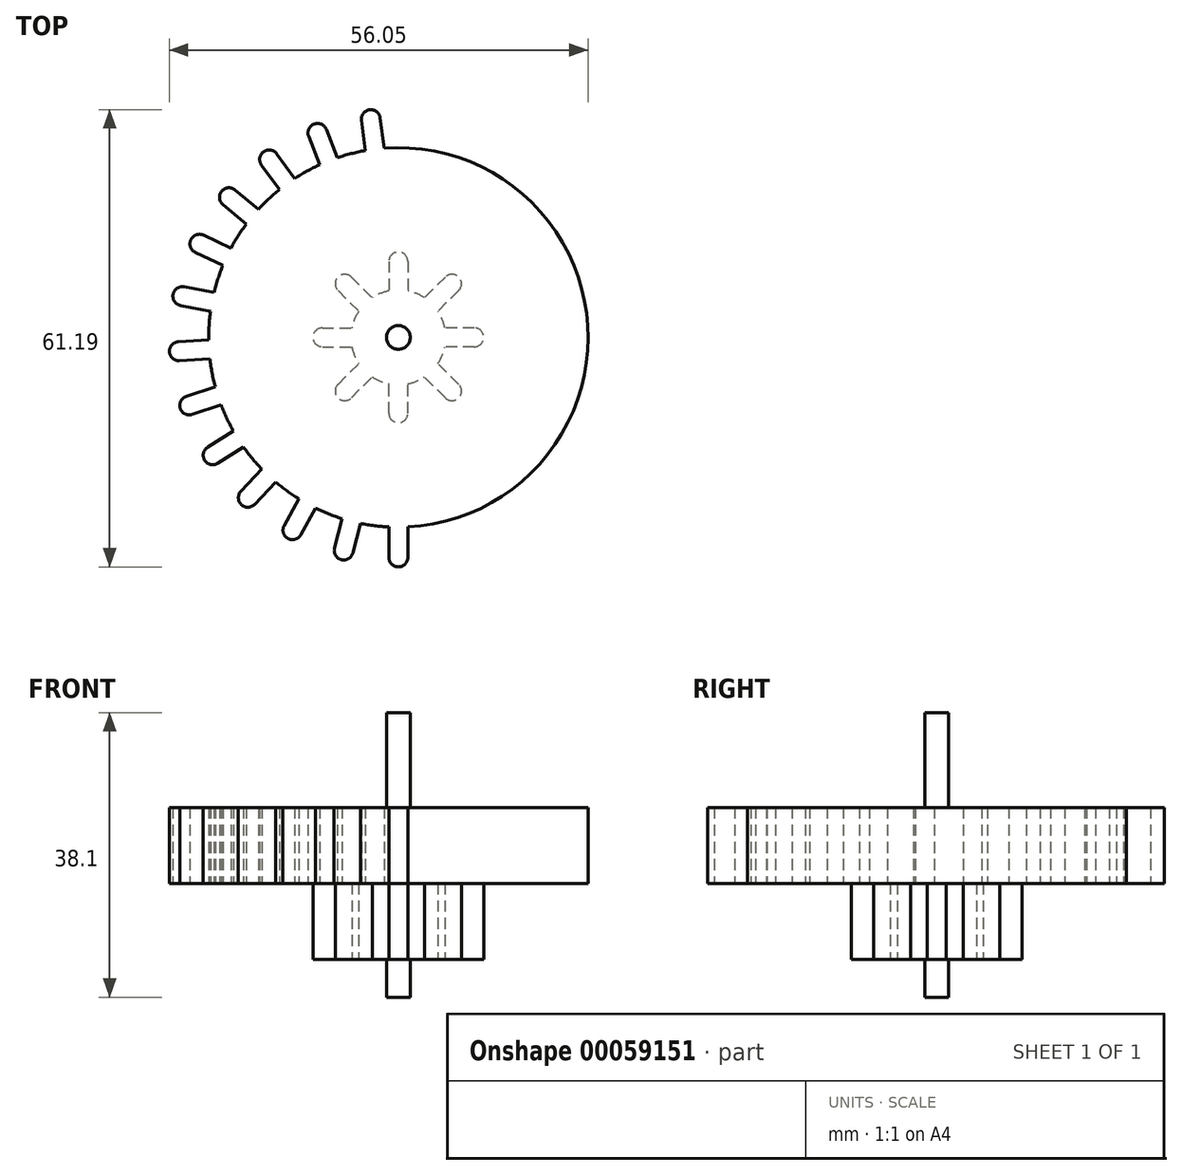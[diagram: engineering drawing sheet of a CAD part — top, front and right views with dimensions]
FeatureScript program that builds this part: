
annotation { "Feature Type Name" : "Feature", "Feature Type Description" : "" }
export const myFeature = defineFeature(function(context is Context, id is Id, definition is map)
    precondition{}
    {
        {
            var Q0;
            Q0=qCreatedBy(makeId("Top.planeOp"),FACE);
            var sketch = newSketch(context, id + "F0", { "sketchPlane" : qUnion([Q0])});
            skCircle(sketch, "E0", {"center": v(0, 0) * mm, "radius": 6.35 * mm});
            skLineSegment(sketch, "E1", {"start": v(0, 10.16) * mm, "end": v(1.27, 10.16) * mm});
            skLineSegment(sketch, "E2.MirrorCS", {"start": v(0, 10.16) * mm, "end": v(-1.27, 10.16) * mm});
            skLineSegment(sketch, "E3", {"start": v(-1.27, 10.16) * mm, "end": v(-1.27, 6.22) * mm});
            skLineSegment(sketch, "E4", {"start": v(1.27, 10.16) * mm, "end": v(1.27, 6.22) * mm});
            skArc(sketch, "E5", {"start": v(1.27, 10.16) * mm, "mid": v(0, 11.43) * mm, "end": v(-1.27, 10.16) * mm});
            skLineSegment(sketch, "E6.1.0", {"start": v(-6.29, 8.08) * mm, "end": v(-3.5, 5.3) * mm});
            skArc(sketch, "E6.1.1", {"start": v(-6.29, 8.08) * mm, "mid": v(-8.08, 8.08) * mm, "end": v(-8.08, 6.29) * mm});
            skLineSegment(sketch, "E6.1.2", {"start": v(-8.08, 6.29) * mm, "end": v(-5.3, 3.5) * mm});
            skLineSegment(sketch, "E6.2.0", {"start": v(-10.16, 1.27) * mm, "end": v(-6.22, 1.27) * mm});
            skArc(sketch, "E6.2.1", {"start": v(-10.16, 1.27) * mm, "mid": v(-11.43, 0) * mm, "end": v(-10.16, -1.27) * mm});
            skLineSegment(sketch, "E6.2.2", {"start": v(-10.16, -1.27) * mm, "end": v(-6.22, -1.27) * mm});
            skLineSegment(sketch, "E6.3.0", {"start": v(-8.08, -6.29) * mm, "end": v(-5.3, -3.5) * mm});
            skArc(sketch, "E6.3.1", {"start": v(-8.08, -6.29) * mm, "mid": v(-8.08, -8.08) * mm, "end": v(-6.29, -8.08) * mm});
            skLineSegment(sketch, "E6.3.2", {"start": v(-6.29, -8.08) * mm, "end": v(-3.5, -5.3) * mm});
            skLineSegment(sketch, "E6.4.0", {"start": v(-1.27, -10.16) * mm, "end": v(-1.27, -6.22) * mm});
            skArc(sketch, "E6.4.1", {"start": v(-1.27, -10.16) * mm, "mid": v(0, -11.43) * mm, "end": v(1.27, -10.16) * mm});
            skLineSegment(sketch, "E6.4.2", {"start": v(1.27, -10.16) * mm, "end": v(1.27, -6.22) * mm});
            skLineSegment(sketch, "E6.5.0", {"start": v(6.29, -8.08) * mm, "end": v(3.5, -5.3) * mm});
            skArc(sketch, "E6.5.1", {"start": v(6.29, -8.08) * mm, "mid": v(8.08, -8.08) * mm, "end": v(8.08, -6.29) * mm});
            skLineSegment(sketch, "E6.5.2", {"start": v(8.08, -6.29) * mm, "end": v(5.3, -3.5) * mm});
            skLineSegment(sketch, "E7.2.6.0", {"start": v(10.16, -1.27) * mm, "end": v(6.22, -1.27) * mm});
            skArc(sketch, "E7.3.6.0", {"start": v(10.16, -1.27) * mm, "mid": v(11.43, 0) * mm, "end": v(10.16, 1.27) * mm});
            skLineSegment(sketch, "E7.7.6.0", {"start": v(10.16, 1.27) * mm, "end": v(6.22, 1.27) * mm});
            skLineSegment(sketch, "E7.2.7.0", {"start": v(8.08, 6.29) * mm, "end": v(5.3, 3.5) * mm});
            skArc(sketch, "E7.3.7.0", {"start": v(8.08, 6.29) * mm, "mid": v(8.08, 8.08) * mm, "end": v(6.29, 8.08) * mm});
            skLineSegment(sketch, "E7.7.7.0", {"start": v(6.29, 8.08) * mm, "end": v(3.5, 5.3) * mm});
            skSolve(sketch);
        }
        {
            var Q0;
            {var subQ0=sQuery(id+"F0.wireOp",EDGE,"E0");var subQ3=makeQuery(id+"F0.imprint","INTERSECT",VERTEX,{"derivedFrom":[subQ0,sQuery(id+"F0.wireOp",EDGE,"E6.6.2")]});Q0=makeQuery(id+"F0.imprint","IMPRINT",FACE,{"disambiguationData":[TD([[makeQuery(id+"F0.imprint","IMPRINT",EDGE,{"disambiguationData":[TD([[subQ3,-1.0]])],"derivedFrom":subQ0}),1.0]])]});}
            var Q1;
            {var subQ0=sQuery(id+"F0.wireOp",EDGE,"E6.1.0");Q1=makeQuery(id+"F0.imprint","IMPRINT",FACE,{"disambiguationData":[TD([[makeQuery(id+"F0.imprint","IMPRINT",EDGE,{"derivedFrom":subQ0}),-1.0]])]});}
            var Q2;
            Q2=makeQuery(id+"F0.imprint","IMPRINT",FACE,{"disambiguationData":[TD([[makeQuery(id+"F0.imprint","IMPRINT",EDGE,{"derivedFrom":sQuery(id+"F0.wireOp",EDGE,"E1")}),-1.0]])]});
            var Q3;
            {var subQ0=sQuery(id+"F0.wireOp",EDGE,"E6.7.0");Q3=makeQuery(id+"F0.imprint","IMPRINT",FACE,{"disambiguationData":[TD([[makeQuery(id+"F0.imprint","IMPRINT",EDGE,{"derivedFrom":subQ0}),-1.0]])]});}
            var Q4;
            {var subQ0=sQuery(id+"F0.wireOp",EDGE,"E6.6.0");Q4=makeQuery(id+"F0.imprint","IMPRINT",FACE,{"disambiguationData":[TD([[makeQuery(id+"F0.imprint","IMPRINT",EDGE,{"derivedFrom":subQ0}),-1.0]])]});}
            var Q5;
            Q5=makeQuery(id+"F0.imprint","IMPRINT",FACE,{"disambiguationData":[TD([[makeQuery(id+"F0.imprint","IMPRINT",EDGE,{"derivedFrom":sQuery(id+"F0.wireOp",EDGE,"E1")}),1.0]])]});
            var Q6;
            {var subQ0=sQuery(id+"F0.wireOp",EDGE,"E6.2.0");Q6=makeQuery(id+"F0.imprint","IMPRINT",FACE,{"disambiguationData":[TD([[makeQuery(id+"F0.imprint","IMPRINT",EDGE,{"derivedFrom":subQ0}),-1.0]])]});}
            var Q7;
            {var subQ0=sQuery(id+"F0.wireOp",EDGE,"E6.3.0");Q7=makeQuery(id+"F0.imprint","IMPRINT",FACE,{"disambiguationData":[TD([[makeQuery(id+"F0.imprint","IMPRINT",EDGE,{"derivedFrom":subQ0}),-1.0]])]});}
            var Q8;
            {var subQ0=sQuery(id+"F0.wireOp",EDGE,"E6.4.0");Q8=makeQuery(id+"F0.imprint","IMPRINT",FACE,{"disambiguationData":[TD([[makeQuery(id+"F0.imprint","IMPRINT",EDGE,{"derivedFrom":subQ0}),-1.0]])]});}
            var Q9;
            {var subQ0=sQuery(id+"F0.wireOp",EDGE,"E6.5.0");Q9=makeQuery(id+"F0.imprint","IMPRINT",FACE,{"disambiguationData":[TD([[makeQuery(id+"F0.imprint","IMPRINT",EDGE,{"derivedFrom":subQ0}),-1.0]])]});}
            var Q10;
            {var subQ0=sQuery(id+"F0.wireOp",EDGE,"E7.2.6.0");Q10=makeQuery(id+"F0.imprint","IMPRINT",FACE,{"disambiguationData":[TD([[makeQuery(id+"F0.imprint","IMPRINT",EDGE,{"derivedFrom":subQ0}),-1.0]])]});}
            var Q11;
            {var subQ0=sQuery(id+"F0.wireOp",EDGE,"E7.2.7.0");Q11=makeQuery(id+"F0.imprint","IMPRINT",FACE,{"disambiguationData":[TD([[makeQuery(id+"F0.imprint","IMPRINT",EDGE,{"derivedFrom":subQ0}),-1.0]])]});}
            extrude(context, id + "F1", {"entities" : qUnion([Q0, Q1, Q2, Q3, Q4, Q5, Q6, Q7, Q8, Q9, Q10, Q11]), "depth" : 10.16 * mm});
        }
        {
            var Q0;
            Q0=makeQuery(id+"F1.opExtrude","CAP_FACE",FACE,{"disambiguationData":[OSD([sQuery(id+"F0.wireOp",EDGE,"E0"),sQuery(id+"F0.wireOp",EDGE,"E3"),sQuery(id+"F0.wireOp",EDGE,"E4"),sQuery(id+"F0.wireOp",EDGE,"E5"),sQuery(id+"F0.wireOp",EDGE,"E6.1.0"),sQuery(id+"F0.wireOp",EDGE,"E6.1.1"),sQuery(id+"F0.wireOp",EDGE,"E6.1.2"),sQuery(id+"F0.wireOp",EDGE,"E6.2.0"),sQuery(id+"F0.wireOp",EDGE,"E6.2.1"),sQuery(id+"F0.wireOp",EDGE,"E6.2.2"),sQuery(id+"F0.wireOp",EDGE,"E6.3.0"),sQuery(id+"F0.wireOp",EDGE,"E6.3.1"),sQuery(id+"F0.wireOp",EDGE,"E6.3.2"),sQuery(id+"F0.wireOp",EDGE,"E6.4.0"),sQuery(id+"F0.wireOp",EDGE,"E6.4.1"),sQuery(id+"F0.wireOp",EDGE,"E6.4.2"),sQuery(id+"F0.wireOp",EDGE,"E6.5.0"),sQuery(id+"F0.wireOp",EDGE,"E6.5.1"),sQuery(id+"F0.wireOp",EDGE,"E6.5.2"),sQuery(id+"F0.wireOp",EDGE,"E6.6.0"),sQuery(id+"F0.wireOp",EDGE,"E6.6.1"),sQuery(id+"F0.wireOp",EDGE,"E6.6.2"),sQuery(id+"F0.wireOp",EDGE,"E6.7.0"),sQuery(id+"F0.wireOp",EDGE,"E6.7.1"),sQuery(id+"F0.wireOp",EDGE,"E6.7.2")])],"isStart":false});
            var sketch = newSketch(context, id + "F2", { "sketchPlane" : qUnion([Q0])});
            skPoint(sketch, "E8.center", {"position": v(0, 0) * mm});
            skCircle(sketch, "E9", {"center": v(0, 0) * mm, "radius": 25.4 * mm});
            skLineSegment(sketch, "E8.17.0", {"start": v(28.4, -7.9) * mm, "end": v(24.52, -6.63) * mm});
            skLineSegment(sketch, "E8.17.1", {"start": v(27.6, -10.3) * mm, "end": v(23.73, -9.05) * mm});
            skArc(sketch, "E8.17.2", {"start": v(27.6, -10.3) * mm, "mid": v(29.2, -9.5) * mm, "end": v(28.4, -7.9) * mm});
            skLineSegment(sketch, "E8.14.0", {"start": v(15.3, -25.19) * mm, "end": v(13.33, -21.62) * mm});
            skLineSegment(sketch, "E8.14.1", {"start": v(13.07, -26.41) * mm, "end": v(11.1, -22.84) * mm});
            skArc(sketch, "E8.14.2", {"start": v(13.07, -26.41) * mm, "mid": v(14.8, -26.91) * mm, "end": v(15.3, -25.19) * mm});
            skLineSegment(sketch, "E8.4.0", {"start": v(-27.18, 11.39) * mm, "end": v(-23.5, 9.65) * mm});
            skLineSegment(sketch, "E8.1.0", {"start": v(-12.02, 26.9) * mm, "end": v(-10.52, 23.12) * mm});
            skLineSegment(sketch, "E8.1.1", {"start": v(-9.66, 27.84) * mm, "end": v(-8.16, 24.05) * mm});
            skArc(sketch, "E8.1.2", {"start": v(-9.66, 27.84) * mm, "mid": v(-11.3, 28.56) * mm, "end": v(-12.02, 26.9) * mm});
            skLineSegment(sketch, "E8.2.0", {"start": v(-18.33, 23.07) * mm, "end": v(-15.94, 19.78) * mm});
            skLineSegment(sketch, "E8.2.1", {"start": v(-16.28, 24.57) * mm, "end": v(-13.88, 21.27) * mm});
            skArc(sketch, "E8.2.2", {"start": v(-16.28, 24.57) * mm, "mid": v(-18.05, 24.85) * mm, "end": v(-18.33, 23.07) * mm});
            skLineSegment(sketch, "E8.4.1", {"start": v(-26.1, 13.68) * mm, "end": v(-22.41, 11.95) * mm});
            skArc(sketch, "E8.4.2", {"start": v(-26.1, 13.68) * mm, "mid": v(-27.79, 13.08) * mm, "end": v(-27.18, 11.39) * mm});
            skLineSegment(sketch, "E8.5.1", {"start": v(-28.68, 6.76) * mm, "end": v(-24.68, 6) * mm});
            skLineSegment(sketch, "E10.3.21.0", {"start": v(23.5, 17.79) * mm, "end": v(20.36, 15.2) * mm});
            skLineSegment(sketch, "E8.16.0", {"start": v(25.54, -14.7) * mm, "end": v(22.1, -12.52) * mm});
            skArc(sketch, "E8.10.2", {"start": v(-15.3, -25.19) * mm, "mid": v(-14.8, -26.91) * mm, "end": v(-13.07, -26.41) * mm});
            skArc(sketch, "E8.5.2", {"start": v(-28.68, 6.76) * mm, "mid": v(-30.17, 5.75) * mm, "end": v(-29.16, 4.27) * mm});
            skArc(sketch, "E10.6.21.0", {"start": v(23.5, 17.79) * mm, "mid": v(23.66, 19.58) * mm, "end": v(21.88, 19.75) * mm});
            skLineSegment(sketch, "E8.16.1", {"start": v(24.18, -16.85) * mm, "end": v(20.74, -14.67) * mm});
            skLineSegment(sketch, "E8.11.0", {"start": v(-6.1, -28.83) * mm, "end": v(-5.08, -24.89) * mm});
            skArc(sketch, "E8.16.2", {"start": v(24.18, -16.85) * mm, "mid": v(25.93, -16.46) * mm, "end": v(25.54, -14.7) * mm});
            skLineSegment(sketch, "E8.11.1", {"start": v(-8.55, -28.2) * mm, "end": v(-7.54, -24.26) * mm});
            skArc(sketch, "E8.11.2", {"start": v(-8.55, -28.2) * mm, "mid": v(-7.64, -29.75) * mm, "end": v(-6.1, -28.83) * mm});
            skLineSegment(sketch, "E8.12.0", {"start": v(1.27, -29.44) * mm, "end": v(1.27, -25.37) * mm});
            skLineSegment(sketch, "E8.12.1", {"start": v(-1.27, -29.44) * mm, "end": v(-1.27, -25.37) * mm});
            skLineSegment(sketch, "E8.7.0", {"start": v(-27.6, -10.3) * mm, "end": v(-23.73, -9.05) * mm});
            skLineSegment(sketch, "E8.18.0", {"start": v(29.46, -0.58) * mm, "end": v(25.4, -0.33) * mm});
            skArc(sketch, "E8.12.2", {"start": v(-1.27, -29.44) * mm, "mid": v(0, -30.71) * mm, "end": v(1.27, -29.44) * mm});
            skLineSegment(sketch, "E8.18.1", {"start": v(29.3, -3.12) * mm, "end": v(25.24, -2.86) * mm});
            skLineSegment(sketch, "E8.13.0", {"start": v(8.55, -28.2) * mm, "end": v(7.54, -24.26) * mm});
            skArc(sketch, "E8.7.2", {"start": v(-28.4, -7.9) * mm, "mid": v(-29.2, -9.5) * mm, "end": v(-27.6, -10.3) * mm});
            skArc(sketch, "E8.18.2", {"start": v(29.3, -3.12) * mm, "mid": v(30.65, -1.93) * mm, "end": v(29.46, -0.58) * mm});
            skLineSegment(sketch, "E8.13.1", {"start": v(6.1, -28.83) * mm, "end": v(5.08, -24.89) * mm});
            skLineSegment(sketch, "E8.8.0", {"start": v(-24.18, -16.85) * mm, "end": v(-20.74, -14.67) * mm});
            skLineSegment(sketch, "E11.2.24.0", {"start": v(2.43, 29.37) * mm, "end": v(1.92, 25.33) * mm});
            skArc(sketch, "E11.6.24.0", {"start": v(4.95, 29.05) * mm, "mid": v(3.85, 30.47) * mm, "end": v(2.43, 29.37) * mm});
            skArc(sketch, "E8.8.2", {"start": v(-25.54, -14.7) * mm, "mid": v(-25.93, -16.46) * mm, "end": v(-24.18, -16.85) * mm});
            skArc(sketch, "E8.13.2", {"start": v(6.1, -28.83) * mm, "mid": v(7.64, -29.75) * mm, "end": v(8.55, -28.2) * mm});
            skLineSegment(sketch, "E8.8.1", {"start": v(-25.54, -14.7) * mm, "end": v(-22.1, -12.52) * mm});
            skLineSegment(sketch, "E11.3.24.0", {"start": v(4.95, 29.05) * mm, "end": v(4.44, 25) * mm});
            skLineSegment(sketch, "E8.9.0", {"start": v(-19.23, -22.33) * mm, "end": v(-16.44, -19.36) * mm});
            skLineSegment(sketch, "E10.2.20.0", {"start": v(26.1, 13.68) * mm, "end": v(22.41, 11.95) * mm});
            skLineSegment(sketch, "E8.9.1", {"start": v(-21.08, -20.6) * mm, "end": v(-18.3, -17.62) * mm});
            skLineSegment(sketch, "E8.3.1", {"start": v(-21.88, 19.75) * mm, "end": v(-18.74, 17.15) * mm});
            skArc(sketch, "E8.3.2", {"start": v(-21.88, 19.75) * mm, "mid": v(-23.66, 19.58) * mm, "end": v(-23.5, 17.79) * mm});
            skLineSegment(sketch, "E8.3.0", {"start": v(-23.5, 17.79) * mm, "end": v(-20.36, 15.2) * mm});
            skLineSegment(sketch, "E8.15.0", {"start": v(21.08, -20.6) * mm, "end": v(18.3, -17.62) * mm});
            skArc(sketch, "E8.9.2", {"start": v(-21.08, -20.6) * mm, "mid": v(-21.02, -22.39) * mm, "end": v(-19.23, -22.33) * mm});
            skArc(sketch, "E10.6.20.0", {"start": v(27.18, 11.39) * mm, "mid": v(27.79, 13.08) * mm, "end": v(26.1, 13.68) * mm});
            skLineSegment(sketch, "E8.15.1", {"start": v(19.23, -22.33) * mm, "end": v(16.44, -19.36) * mm});
            skLineSegment(sketch, "E8.10.0", {"start": v(-13.07, -26.41) * mm, "end": v(-11.1, -22.84) * mm});
            skLineSegment(sketch, "E8.5.0", {"start": v(-29.16, 4.27) * mm, "end": v(-25.16, 3.5) * mm});
            skLineSegment(sketch, "E10.2.21.0", {"start": v(21.88, 19.75) * mm, "end": v(18.74, 17.15) * mm});
            skArc(sketch, "E8.15.2", {"start": v(19.23, -22.33) * mm, "mid": v(21.02, -22.39) * mm, "end": v(21.08, -20.6) * mm});
            skLineSegment(sketch, "E8.10.1", {"start": v(-15.3, -25.19) * mm, "end": v(-13.33, -21.62) * mm});
            skLineSegment(sketch, "E8.6.0", {"start": v(-29.3, -3.12) * mm, "end": v(-25.24, -2.86) * mm});
            skLineSegment(sketch, "E11.2.22.0", {"start": v(16.28, 24.57) * mm, "end": v(13.88, 21.27) * mm});
            skLineSegment(sketch, "E8.6.1", {"start": v(-29.46, -0.58) * mm, "end": v(-25.4, -0.33) * mm});
            skLineSegment(sketch, "E11.3.22.0", {"start": v(18.33, 23.07) * mm, "end": v(15.94, 19.78) * mm});
            skArc(sketch, "E8.6.2", {"start": v(-29.46, -0.58) * mm, "mid": v(-30.65, -1.93) * mm, "end": v(-29.3, -3.12) * mm});
            skArc(sketch, "E11.6.22.0", {"start": v(18.33, 23.07) * mm, "mid": v(18.05, 24.85) * mm, "end": v(16.28, 24.57) * mm});
            skLineSegment(sketch, "E11.2.23.0", {"start": v(9.66, 27.84) * mm, "end": v(8.16, 24.05) * mm});
            skLineSegment(sketch, "E8.7.1", {"start": v(-28.4, -7.9) * mm, "end": v(-24.52, -6.63) * mm});
            skLineSegment(sketch, "E11.3.23.0", {"start": v(12.02, 26.9) * mm, "end": v(10.52, 23.12) * mm});
            skArc(sketch, "E11.6.23.0", {"start": v(12.02, 26.9) * mm, "mid": v(11.3, 28.56) * mm, "end": v(9.66, 27.84) * mm});
            skLineSegment(sketch, "E8.19.1", {"start": v(29.16, 4.27) * mm, "end": v(25.16, 3.5) * mm});
            skLineSegment(sketch, "E8.19.0", {"start": v(28.68, 6.76) * mm, "end": v(24.68, 6) * mm});
            skArc(sketch, "E8.19.2", {"start": v(29.16, 4.27) * mm, "mid": v(30.17, 5.75) * mm, "end": v(28.68, 6.76) * mm});
            skLineSegment(sketch, "E12", {"start": v(-4.95, 29.05) * mm, "end": v(-4.44, 25) * mm});
            skLineSegment(sketch, "E13", {"start": v(-2.43, 29.37) * mm, "end": v(-1.92, 25.33) * mm});
            skArc(sketch, "E14", {"start": v(-2.43, 29.37) * mm, "mid": v(-3.85, 30.47) * mm, "end": v(-4.95, 29.05) * mm});
            skLineSegment(sketch, "E10.3.20.0", {"start": v(27.18, 11.39) * mm, "end": v(23.5, 9.65) * mm});
            skLineSegment(sketch, "E15", {"start": v(-3.7, 29.2) * mm, "end": v(-4.95, 29.05) * mm});
            skLineSegment(sketch, "E16.MirrorCS", {"start": v(-3.7, 29.21) * mm, "end": v(-2.43, 29.37) * mm});
            skSolve(sketch);
        }
        {
            var Q0;
            {var subQ5=sQuery(id+"F2.wireOp",EDGE,"b0236bb4-0209-4acc-8ecc-2f9dec660ae4.1.2");Q0=makeQuery(id+"F2.imprint","IMPRINT",FACE,{"disambiguationData":[TD([[makeQuery(id+"F2.imprint","IMPRINT",EDGE,{"derivedFrom":subQ5}),1.0]])]});}
            var Q1;
            {var subQ5=sQuery(id+"F2.wireOp",EDGE,"b0236bb4-0209-4acc-8ecc-2f9dec660ae4.2.2");Q1=makeQuery(id+"F2.imprint","IMPRINT",FACE,{"disambiguationData":[TD([[makeQuery(id+"F2.imprint","IMPRINT",EDGE,{"derivedFrom":subQ5}),1.0]])]});}
            var Q2;
            {var subQ5=sQuery(id+"F2.wireOp",EDGE,"b0236bb4-0209-4acc-8ecc-2f9dec660ae4.3.2");Q2=makeQuery(id+"F2.imprint","IMPRINT",FACE,{"disambiguationData":[TD([[makeQuery(id+"F2.imprint","IMPRINT",EDGE,{"derivedFrom":subQ5}),1.0]])]});}
            var Q3;
            {var subQ5=sQuery(id+"F2.wireOp",EDGE,"b0236bb4-0209-4acc-8ecc-2f9dec660ae4.4.2");Q3=makeQuery(id+"F2.imprint","IMPRINT",FACE,{"disambiguationData":[TD([[makeQuery(id+"F2.imprint","IMPRINT",EDGE,{"derivedFrom":subQ5}),1.0]])]});}
            var Q4;
            {var subQ5=sQuery(id+"F2.wireOp",EDGE,"b0236bb4-0209-4acc-8ecc-2f9dec660ae4.5.2");Q4=makeQuery(id+"F2.imprint","IMPRINT",FACE,{"disambiguationData":[TD([[makeQuery(id+"F2.imprint","IMPRINT",EDGE,{"derivedFrom":subQ5}),1.0]])]});}
            var Q5;
            {var subQ5=sQuery(id+"F2.wireOp",EDGE,"b0236bb4-0209-4acc-8ecc-2f9dec660ae4.6.2");Q5=makeQuery(id+"F2.imprint","IMPRINT",FACE,{"disambiguationData":[TD([[makeQuery(id+"F2.imprint","IMPRINT",EDGE,{"derivedFrom":subQ5}),1.0]])]});}
            var Q6;
            {var subQ5=sQuery(id+"F2.wireOp",EDGE,"b0236bb4-0209-4acc-8ecc-2f9dec660ae4.7.2");Q6=makeQuery(id+"F2.imprint","IMPRINT",FACE,{"disambiguationData":[TD([[makeQuery(id+"F2.imprint","IMPRINT",EDGE,{"derivedFrom":subQ5}),1.0]])]});}
            var Q7;
            {var subQ5=sQuery(id+"F2.wireOp",EDGE,"b0236bb4-0209-4acc-8ecc-2f9dec660ae4.8.2");Q7=makeQuery(id+"F2.imprint","IMPRINT",FACE,{"disambiguationData":[TD([[makeQuery(id+"F2.imprint","IMPRINT",EDGE,{"derivedFrom":subQ5}),1.0]])]});}
            var Q8;
            {var subQ5=sQuery(id+"F2.wireOp",EDGE,"b0236bb4-0209-4acc-8ecc-2f9dec660ae4.9.2");Q8=makeQuery(id+"F2.imprint","IMPRINT",FACE,{"disambiguationData":[TD([[makeQuery(id+"F2.imprint","IMPRINT",EDGE,{"derivedFrom":subQ5}),1.0]])]});}
            var Q9;
            {var subQ5=sQuery(id+"F2.wireOp",EDGE,"b0236bb4-0209-4acc-8ecc-2f9dec660ae4.10.2");Q9=makeQuery(id+"F2.imprint","IMPRINT",FACE,{"disambiguationData":[TD([[makeQuery(id+"F2.imprint","IMPRINT",EDGE,{"derivedFrom":subQ5}),1.0]])]});}
            var Q10;
            {var subQ5=sQuery(id+"F2.wireOp",EDGE,"b0236bb4-0209-4acc-8ecc-2f9dec660ae4.11.2");Q10=makeQuery(id+"F2.imprint","IMPRINT",FACE,{"disambiguationData":[TD([[makeQuery(id+"F2.imprint","IMPRINT",EDGE,{"derivedFrom":subQ5}),1.0]])]});}
            var Q11;
            Q11=makeQuery(id+"F2.imprint","IMPRINT",FACE,{"disambiguationData":[TD([[makeQuery(id+"F2.imprint","IMPRINT",EDGE,{"derivedFrom":sQuery(id+"F2.wireOp",EDGE,"a617dc30-04bb-4b02-898b-82f21cb4bea1")}),1.0]])]});
            var Q12;
            {var subQ11=sQuery(id+"F0.wireOp",EDGE,"E3");Q12=makeQuery(id+"F2.imprint","IMPRINT",FACE,{"disambiguationData":[TD([[makeQuery(id+"F2.imprint","IMPRINT",EDGE,{"derivedFrom":makeQuery(id+"F1.opExtrude","CAP_EDGE",EDGE,{"disambiguationData":[OSD([subQ11])],"isStart":false})}),1.0]])]});}
            var Q13;
            {var subQ1=sQuery(id+"F2.wireOp",EDGE,"a3267446-eaba-4b86-878d-2723d5209084");Q13=makeQuery(id+"F2.imprint","IMPRINT",FACE,{"disambiguationData":[TD([[makeQuery(id+"F2.imprint","IMPRINT",EDGE,{"derivedFrom":subQ1}),1.0]])]});}
            var Q14;
            {var subQ22=sQuery(id+"F0.wireOp",EDGE,"E3");Q14=makeQuery(id+"F2.imprint","IMPRINT",FACE,{"disambiguationData":[TD([[makeQuery(id+"F2.imprint","IMPRINT",EDGE,{"derivedFrom":makeQuery(id+"F1.opExtrude","CAP_EDGE",EDGE,{"disambiguationData":[OSD([subQ22])],"isStart":false})}),-1.0]])]});}
            var Q15;
            {var subQ5=sQuery(id+"F2.wireOp",EDGE,"b0236bb4-0209-4acc-8ecc-2f9dec660ae4.12.2");Q15=makeQuery(id+"F2.imprint","IMPRINT",FACE,{"disambiguationData":[TD([[makeQuery(id+"F2.imprint","IMPRINT",EDGE,{"derivedFrom":subQ5}),1.0]])]});}
            var Q16;
            {var subQ5=sQuery(id+"F2.wireOp",EDGE,"E8.4.2");Q16=makeQuery(id+"F2.imprint","IMPRINT",FACE,{"disambiguationData":[TD([[makeQuery(id+"F2.imprint","IMPRINT",EDGE,{"derivedFrom":subQ5}),1.0]])]});}
            var Q17;
            {var subQ5=sQuery(id+"F2.wireOp",EDGE,"E8.3.2");Q17=makeQuery(id+"F2.imprint","IMPRINT",FACE,{"disambiguationData":[TD([[makeQuery(id+"F2.imprint","IMPRINT",EDGE,{"derivedFrom":subQ5}),1.0]])]});}
            var Q18;
            {var subQ5=sQuery(id+"F2.wireOp",EDGE,"E8.2.2");Q18=makeQuery(id+"F2.imprint","IMPRINT",FACE,{"disambiguationData":[TD([[makeQuery(id+"F2.imprint","IMPRINT",EDGE,{"derivedFrom":subQ5}),1.0]])]});}
            var Q19;
            {var subQ5=sQuery(id+"F2.wireOp",EDGE,"E8.1.2");Q19=makeQuery(id+"F2.imprint","IMPRINT",FACE,{"disambiguationData":[TD([[makeQuery(id+"F2.imprint","IMPRINT",EDGE,{"derivedFrom":subQ5}),1.0]])]});}
            var Q20;
            {var subQ1=sQuery(id+"F2.wireOp",EDGE,"E12");Q20=makeQuery(id+"F2.imprint","IMPRINT",FACE,{"disambiguationData":[TD([[makeQuery(id+"F2.imprint","IMPRINT",EDGE,{"derivedFrom":subQ1}),1.0]])]});}
            var Q21;
            {var subQ5=sQuery(id+"F2.wireOp",EDGE,"E8.5.2");Q21=makeQuery(id+"F2.imprint","IMPRINT",FACE,{"disambiguationData":[TD([[makeQuery(id+"F2.imprint","IMPRINT",EDGE,{"derivedFrom":subQ5}),1.0]])]});}
            var Q22;
            {var subQ5=sQuery(id+"F2.wireOp",EDGE,"E8.6.2");Q22=makeQuery(id+"F2.imprint","IMPRINT",FACE,{"disambiguationData":[TD([[makeQuery(id+"F2.imprint","IMPRINT",EDGE,{"derivedFrom":subQ5}),1.0]])]});}
            var Q23;
            {var subQ5=sQuery(id+"F2.wireOp",EDGE,"E8.7.2");Q23=makeQuery(id+"F2.imprint","IMPRINT",FACE,{"disambiguationData":[TD([[makeQuery(id+"F2.imprint","IMPRINT",EDGE,{"derivedFrom":subQ5}),1.0]])]});}
            var Q24;
            {var subQ5=sQuery(id+"F2.wireOp",EDGE,"E8.8.2");Q24=makeQuery(id+"F2.imprint","IMPRINT",FACE,{"disambiguationData":[TD([[makeQuery(id+"F2.imprint","IMPRINT",EDGE,{"derivedFrom":subQ5}),1.0]])]});}
            var Q25;
            {var subQ5=sQuery(id+"F2.wireOp",EDGE,"E8.9.2");Q25=makeQuery(id+"F2.imprint","IMPRINT",FACE,{"disambiguationData":[TD([[makeQuery(id+"F2.imprint","IMPRINT",EDGE,{"derivedFrom":subQ5}),1.0]])]});}
            var Q26;
            {var subQ5=sQuery(id+"F2.wireOp",EDGE,"E8.10.2");Q26=makeQuery(id+"F2.imprint","IMPRINT",FACE,{"disambiguationData":[TD([[makeQuery(id+"F2.imprint","IMPRINT",EDGE,{"derivedFrom":subQ5}),1.0]])]});}
            var Q27;
            {var subQ5=sQuery(id+"F2.wireOp",EDGE,"E8.11.2");Q27=makeQuery(id+"F2.imprint","IMPRINT",FACE,{"disambiguationData":[TD([[makeQuery(id+"F2.imprint","IMPRINT",EDGE,{"derivedFrom":subQ5}),1.0]])]});}
            var Q28;
            {var subQ5=sQuery(id+"F2.wireOp",EDGE,"E8.12.2");Q28=makeQuery(id+"F2.imprint","IMPRINT",FACE,{"disambiguationData":[TD([[makeQuery(id+"F2.imprint","IMPRINT",EDGE,{"derivedFrom":subQ5}),1.0]])]});}
            var Q29;
            Q29=makeQuery(id+"F2.imprint","IMPRINT",FACE,{"disambiguationData":[TD([[makeQuery(id+"F2.imprint","IMPRINT",EDGE,{"derivedFrom":sQuery(id+"F2.wireOp",EDGE,"E14")}),1.0]])]});
            extrude(context, id + "F3", {"entities" : qUnion([Q0, Q1, Q2, Q3, Q4, Q5, Q6, Q7, Q8, Q9, Q10, Q11, Q12, Q13, Q14, Q15, Q16, Q17, Q18, Q19, Q20, Q21, Q22, Q23, Q24, Q25, Q26, Q27, Q28, Q29]), "operationType" : NewBodyOperationType.ADD, "depth" : 10.16 * mm});
        }
        {
            var Q0;
            Q0=makeQuery(id+"F3.opExtrude","CAP_FACE",FACE,{"disambiguationData":[OSD([sQuery(id+"F2.wireOp",EDGE,"E9"),sQuery(id+"F2.wireOp",EDGE,"E8.4.0"),sQuery(id+"F2.wireOp",EDGE,"E8.1.0"),sQuery(id+"F2.wireOp",EDGE,"E8.1.1"),sQuery(id+"F2.wireOp",EDGE,"E8.1.2"),sQuery(id+"F2.wireOp",EDGE,"E8.2.0"),sQuery(id+"F2.wireOp",EDGE,"E8.2.1"),sQuery(id+"F2.wireOp",EDGE,"E8.2.2"),sQuery(id+"F2.wireOp",EDGE,"E8.4.1"),sQuery(id+"F2.wireOp",EDGE,"E8.4.2"),sQuery(id+"F2.wireOp",EDGE,"E8.5.1"),sQuery(id+"F2.wireOp",EDGE,"E8.10.2"),sQuery(id+"F2.wireOp",EDGE,"E8.5.2"),sQuery(id+"F2.wireOp",EDGE,"E8.11.0"),sQuery(id+"F2.wireOp",EDGE,"E8.11.1"),sQuery(id+"F2.wireOp",EDGE,"E8.11.2"),sQuery(id+"F2.wireOp",EDGE,"E8.12.0"),sQuery(id+"F2.wireOp",EDGE,"E8.12.1"),sQuery(id+"F2.wireOp",EDGE,"E8.7.0"),sQuery(id+"F2.wireOp",EDGE,"E8.12.2"),sQuery(id+"F2.wireOp",EDGE,"E8.7.2"),sQuery(id+"F2.wireOp",EDGE,"E8.8.0"),sQuery(id+"F2.wireOp",EDGE,"E8.8.2"),sQuery(id+"F2.wireOp",EDGE,"E8.8.1"),sQuery(id+"F2.wireOp",EDGE,"E8.9.0"),sQuery(id+"F2.wireOp",EDGE,"E8.9.1"),sQuery(id+"F2.wireOp",EDGE,"E8.3.1"),sQuery(id+"F2.wireOp",EDGE,"E8.3.2"),sQuery(id+"F2.wireOp",EDGE,"E8.3.0"),sQuery(id+"F2.wireOp",EDGE,"E8.9.2"),sQuery(id+"F2.wireOp",EDGE,"E8.10.0"),sQuery(id+"F2.wireOp",EDGE,"E8.5.0"),sQuery(id+"F2.wireOp",EDGE,"E8.10.1"),sQuery(id+"F2.wireOp",EDGE,"E8.6.0"),sQuery(id+"F2.wireOp",EDGE,"E8.6.1"),sQuery(id+"F2.wireOp",EDGE,"E8.6.2"),sQuery(id+"F2.wireOp",EDGE,"E8.7.1"),sQuery(id+"F2.wireOp",EDGE,"E12"),sQuery(id+"F2.wireOp",EDGE,"E13"),sQuery(id+"F2.wireOp",EDGE,"E14")])],"isStart":false});
            var sketch = newSketch(context, id + "F4", { "sketchPlane" : qUnion([Q0])});
            skCircle(sketch, "E17", {"center": v(0, 0) * mm, "radius": 1.59 * mm});
            skSolve(sketch);
        }
        {
            var Q0;
            Q0 = qSketchRegion(id + "F4", true);
            extrude(context, id + "F5", {"entities" : qUnion([Q0]), "operationType" : NewBodyOperationType.ADD, "depth" : 12.7 * mm, "hasSecondDirection" : true, "secondDirectionOppositeDirection" : true, "secondDirectionDepth" : 25.4 * mm});
        }
    });
